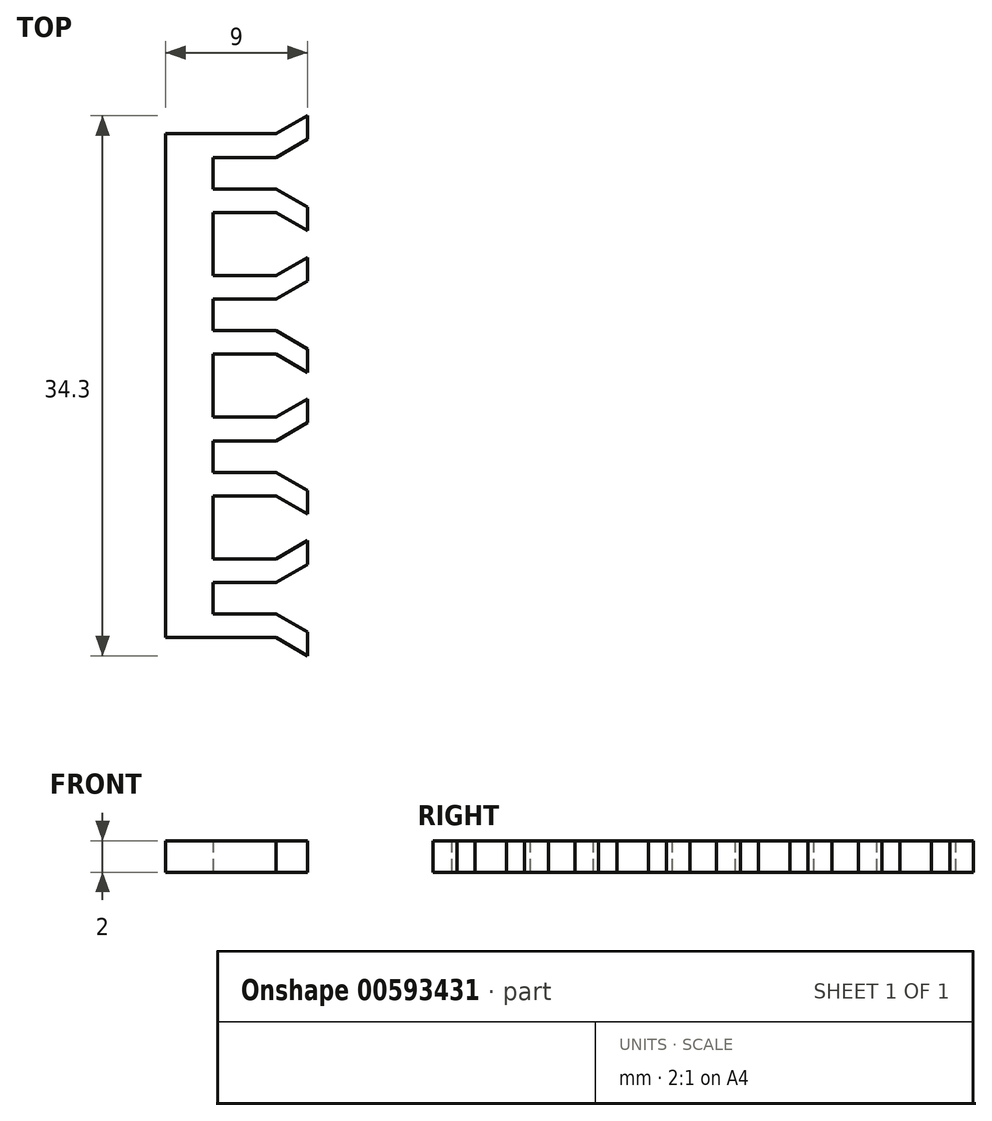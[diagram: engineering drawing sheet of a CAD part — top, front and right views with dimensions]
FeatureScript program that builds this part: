
annotation { "Feature Type Name" : "Feature", "Feature Type Description" : "" }
export const myFeature = defineFeature(function(context is Context, id is Id, definition is map)
    precondition{}
    {
        {
            var Q0;
            Q0=qCreatedBy(makeId("Top.planeOp"),FACE);
            var sketch = newSketch(context, id + "F0", { "sketchPlane" : qUnion([Q0])});
            skLineSegment(sketch, "E0", {"start": v(0, 0) * mm, "end": v(7, 0) * mm});
            skLineSegment(sketch, "E1", {"start": v(7, 0) * mm, "end": v(7, 1.5) * mm});
            skLineSegment(sketch, "E2", {"start": v(7, 1.5) * mm, "end": v(3, 1.5) * mm});
            skLineSegment(sketch, "E3", {"start": v(3, 1.5) * mm, "end": v(3, 3.5) * mm});
            skLineSegment(sketch, "E4", {"start": v(3, 3.5) * mm, "end": v(7, 3.5) * mm});
            skLineSegment(sketch, "E5", {"start": v(7, 3.5) * mm, "end": v(7, 5) * mm});
            skLineSegment(sketch, "E6", {"start": v(7, 5) * mm, "end": v(3, 5) * mm});
            skLineSegment(sketch, "E7", {"start": v(3, 5) * mm, "end": v(3, 9) * mm});
            skLineSegment(sketch, "E8", {"start": v(3, 9) * mm, "end": v(7, 9) * mm});
            skLineSegment(sketch, "E9", {"start": v(7, 9) * mm, "end": v(7, 10.5) * mm});
            skLineSegment(sketch, "E10", {"start": v(7, 10.5) * mm, "end": v(3, 10.5) * mm});
            skLineSegment(sketch, "E11", {"start": v(3, 10.5) * mm, "end": v(3, 12.5) * mm});
            skLineSegment(sketch, "E12", {"start": v(3, 12.5) * mm, "end": v(7, 12.5) * mm});
            skLineSegment(sketch, "E13", {"start": v(7, 12.5) * mm, "end": v(7, 14) * mm});
            skLineSegment(sketch, "E14", {"start": v(7, 14) * mm, "end": v(3, 14) * mm});
            skLineSegment(sketch, "E15", {"start": v(0, 32) * mm, "end": v(0, 0) * mm});
            skLineSegment(sketch, "E16", {"start": v(3, 14) * mm, "end": v(3, 18) * mm});
            skLineSegment(sketch, "E17", {"start": v(3, 18) * mm, "end": v(7, 18) * mm});
            skLineSegment(sketch, "E18", {"start": v(7, 18) * mm, "end": v(7, 19.5) * mm});
            skLineSegment(sketch, "E19", {"start": v(7, 19.5) * mm, "end": v(3, 19.5) * mm});
            skLineSegment(sketch, "E20", {"start": v(3, 19.5) * mm, "end": v(3, 21.5) * mm});
            skLineSegment(sketch, "E21", {"start": v(3, 21.5) * mm, "end": v(7, 21.5) * mm});
            skLineSegment(sketch, "E22", {"start": v(7, 21.5) * mm, "end": v(7, 23) * mm});
            skLineSegment(sketch, "E23", {"start": v(7, 23) * mm, "end": v(3, 23) * mm});
            skLineSegment(sketch, "E24", {"start": v(3, 23) * mm, "end": v(3, 27) * mm});
            skLineSegment(sketch, "E25", {"start": v(3, 27) * mm, "end": v(7, 27) * mm});
            skLineSegment(sketch, "E26", {"start": v(7, 27) * mm, "end": v(7, 28.5) * mm});
            skLineSegment(sketch, "E27", {"start": v(7, 28.5) * mm, "end": v(3, 28.5) * mm});
            skLineSegment(sketch, "E28", {"start": v(3, 28.5) * mm, "end": v(3, 30.5) * mm});
            skLineSegment(sketch, "E29", {"start": v(3, 30.5) * mm, "end": v(7, 30.5) * mm});
            skLineSegment(sketch, "E30", {"start": v(7, 30.5) * mm, "end": v(7, 32) * mm});
            skLineSegment(sketch, "E31", {"start": v(7, 32) * mm, "end": v(0, 32) * mm});
            skSolve(sketch);
        }
        {
            var Q0;
            Q0=qSketchRegion(id+"F0",true);
            extrude(context, id + "F1", {"entities" : qUnion([Q0]), "depth" : 2 * mm, "offsetDistance" : 25 * mm});
        }
        {
            var Q0;
            Q0=makeQuery(id+"F1.opExtrude","CAP_FACE",FACE,{"disambiguationData":[OSD([sQuery(id+"F0.wireOp",EDGE,"E0"),sQuery(id+"F0.wireOp",EDGE,"E1"),sQuery(id+"F0.wireOp",EDGE,"E2"),sQuery(id+"F0.wireOp",EDGE,"E3"),sQuery(id+"F0.wireOp",EDGE,"E4"),sQuery(id+"F0.wireOp",EDGE,"E5"),sQuery(id+"F0.wireOp",EDGE,"E6"),sQuery(id+"F0.wireOp",EDGE,"E7"),sQuery(id+"F0.wireOp",EDGE,"E8"),sQuery(id+"F0.wireOp",EDGE,"E9"),sQuery(id+"F0.wireOp",EDGE,"E10"),sQuery(id+"F0.wireOp",EDGE,"E11"),sQuery(id+"F0.wireOp",EDGE,"E12"),sQuery(id+"F0.wireOp",EDGE,"E13"),sQuery(id+"F0.wireOp",EDGE,"E14"),sQuery(id+"F0.wireOp",EDGE,"E15"),sQuery(id+"F0.wireOp",EDGE,"E16"),sQuery(id+"F0.wireOp",EDGE,"E17"),sQuery(id+"F0.wireOp",EDGE,"E18"),sQuery(id+"F0.wireOp",EDGE,"E19"),sQuery(id+"F0.wireOp",EDGE,"E20"),sQuery(id+"F0.wireOp",EDGE,"E21"),sQuery(id+"F0.wireOp",EDGE,"E22"),sQuery(id+"F0.wireOp",EDGE,"E23"),sQuery(id+"F0.wireOp",EDGE,"E24"),sQuery(id+"F0.wireOp",EDGE,"E25"),sQuery(id+"F0.wireOp",EDGE,"E26"),sQuery(id+"F0.wireOp",EDGE,"E27"),sQuery(id+"F0.wireOp",EDGE,"E28"),sQuery(id+"F0.wireOp",EDGE,"E29"),sQuery(id+"F0.wireOp",EDGE,"E30"),sQuery(id+"F0.wireOp",EDGE,"E31")])],"isStart":false});
            var sketch = newSketch(context, id + "F2", { "sketchPlane" : qUnion([Q0])});
            skLineSegment(sketch, "E32", {"start": v(7, 0) * mm, "end": v(9, -1.15) * mm});
            skLineSegment(sketch, "E33", {"start": v(9, 0.35) * mm, "end": v(7, 1.5) * mm});
            skLineSegment(sketch, "E34", {"start": v(7, 1.5) * mm, "end": v(7, 0) * mm});
            skLineSegment(sketch, "E35", {"start": v(9, -1.15) * mm, "end": v(9, 0.35) * mm});
            skLineSegment(sketch, "E36", {"start": v(3, 2.5) * mm, "end": v(9.04, 2.5) * mm, "construction": true});
            skLineSegment(sketch, "E37.MirrorCS", {"start": v(7, 3.5) * mm, "end": v(7, 5) * mm});
            skLineSegment(sketch, "E38.MirrorCS", {"start": v(9, 6.15) * mm, "end": v(9, 4.65) * mm});
            skLineSegment(sketch, "E39.MirrorCS", {"start": v(9, 4.65) * mm, "end": v(7, 3.5) * mm});
            skLineSegment(sketch, "E40.MirrorCS", {"start": v(7, 5) * mm, "end": v(9, 6.15) * mm});
            skLineSegment(sketch, "E41.1.0.0", {"start": v(9, 13.65) * mm, "end": v(7, 12.5) * mm});
            skLineSegment(sketch, "E41.1.0.1", {"start": v(7, 12.5) * mm, "end": v(7, 14) * mm});
            skLineSegment(sketch, "E41.1.0.2", {"start": v(7, 14) * mm, "end": v(9, 15.15) * mm});
            skLineSegment(sketch, "E41.1.0.3", {"start": v(9, 15.15) * mm, "end": v(9, 13.65) * mm});
            skLineSegment(sketch, "E41.1.0.4", {"start": v(9, 9.35) * mm, "end": v(7, 10.5) * mm});
            skLineSegment(sketch, "E41.1.0.5", {"start": v(7, 9) * mm, "end": v(9, 7.85) * mm});
            skLineSegment(sketch, "E41.1.0.6", {"start": v(7, 10.5) * mm, "end": v(7, 9) * mm});
            skLineSegment(sketch, "E41.1.0.7", {"start": v(9, 7.85) * mm, "end": v(9, 9.35) * mm});
            skLineSegment(sketch, "E41.2.0.0", {"start": v(9, 22.65) * mm, "end": v(7, 21.5) * mm});
            skLineSegment(sketch, "E41.2.0.1", {"start": v(7, 21.5) * mm, "end": v(7, 23) * mm});
            skLineSegment(sketch, "E41.2.0.2", {"start": v(7, 23) * mm, "end": v(9, 24.15) * mm});
            skLineSegment(sketch, "E41.2.0.3", {"start": v(9, 24.15) * mm, "end": v(9, 22.65) * mm});
            skLineSegment(sketch, "E41.2.0.4", {"start": v(9, 18.35) * mm, "end": v(7, 19.5) * mm});
            skLineSegment(sketch, "E41.2.0.5", {"start": v(7, 18) * mm, "end": v(9, 16.85) * mm});
            skLineSegment(sketch, "E41.2.0.6", {"start": v(7, 19.5) * mm, "end": v(7, 18) * mm});
            skLineSegment(sketch, "E41.2.0.7", {"start": v(9, 16.85) * mm, "end": v(9, 18.35) * mm});
            skLineSegment(sketch, "E41.3.0.0", {"start": v(9, 31.65) * mm, "end": v(7, 30.5) * mm});
            skLineSegment(sketch, "E41.3.0.1", {"start": v(7, 30.5) * mm, "end": v(7, 32) * mm});
            skLineSegment(sketch, "E41.3.0.2", {"start": v(7, 32) * mm, "end": v(9, 33.15) * mm});
            skLineSegment(sketch, "E41.3.0.3", {"start": v(9, 33.15) * mm, "end": v(9, 31.65) * mm});
            skLineSegment(sketch, "E41.3.0.4", {"start": v(9, 27.35) * mm, "end": v(7, 28.5) * mm});
            skLineSegment(sketch, "E41.3.0.5", {"start": v(7, 27) * mm, "end": v(9, 25.85) * mm});
            skLineSegment(sketch, "E41.3.0.6", {"start": v(7, 28.5) * mm, "end": v(7, 27) * mm});
            skLineSegment(sketch, "E41.3.0.7", {"start": v(9, 25.85) * mm, "end": v(9, 27.35) * mm});
            skLineSegment(sketch, "E41.direction1", {"start": v(7, 3.5) * mm, "end": v(7, 12.5) * mm, "construction": true});
            skSolve(sketch);
        }
        {
            var Q0;
            Q0 = qSketchRegion(id + "F2", true);
            var Q1;
            Q1=makeQuery(id+"F1.opExtrude","CAP_FACE",FACE,{"disambiguationData":[OSD([sQuery(id+"F0.wireOp",EDGE,"E0"),sQuery(id+"F0.wireOp",EDGE,"E1"),sQuery(id+"F0.wireOp",EDGE,"E2"),sQuery(id+"F0.wireOp",EDGE,"E3"),sQuery(id+"F0.wireOp",EDGE,"E4"),sQuery(id+"F0.wireOp",EDGE,"E5"),sQuery(id+"F0.wireOp",EDGE,"E6"),sQuery(id+"F0.wireOp",EDGE,"E7"),sQuery(id+"F0.wireOp",EDGE,"E8"),sQuery(id+"F0.wireOp",EDGE,"E9"),sQuery(id+"F0.wireOp",EDGE,"E10"),sQuery(id+"F0.wireOp",EDGE,"E11"),sQuery(id+"F0.wireOp",EDGE,"E12"),sQuery(id+"F0.wireOp",EDGE,"E13"),sQuery(id+"F0.wireOp",EDGE,"E14"),sQuery(id+"F0.wireOp",EDGE,"E15"),sQuery(id+"F0.wireOp",EDGE,"E16"),sQuery(id+"F0.wireOp",EDGE,"E17"),sQuery(id+"F0.wireOp",EDGE,"E18"),sQuery(id+"F0.wireOp",EDGE,"E19"),sQuery(id+"F0.wireOp",EDGE,"E20"),sQuery(id+"F0.wireOp",EDGE,"E21"),sQuery(id+"F0.wireOp",EDGE,"E22"),sQuery(id+"F0.wireOp",EDGE,"E23"),sQuery(id+"F0.wireOp",EDGE,"E24"),sQuery(id+"F0.wireOp",EDGE,"E25"),sQuery(id+"F0.wireOp",EDGE,"E26"),sQuery(id+"F0.wireOp",EDGE,"E27"),sQuery(id+"F0.wireOp",EDGE,"E28"),sQuery(id+"F0.wireOp",EDGE,"E29"),sQuery(id+"F0.wireOp",EDGE,"E30"),sQuery(id+"F0.wireOp",EDGE,"E31")])],"isStart":true});
            extrude(context, id + "F3", {"entities" : qUnion([Q0]), "operationType" : NewBodyOperationType.ADD, "endBound" : BoundingType.UP_TO_SURFACE, "oppositeDirection" : true, "depth" : 25 * mm, "endBoundEntityFace" : qUnion([Q1]), "offsetDistance" : 25 * mm});
        }
    });
